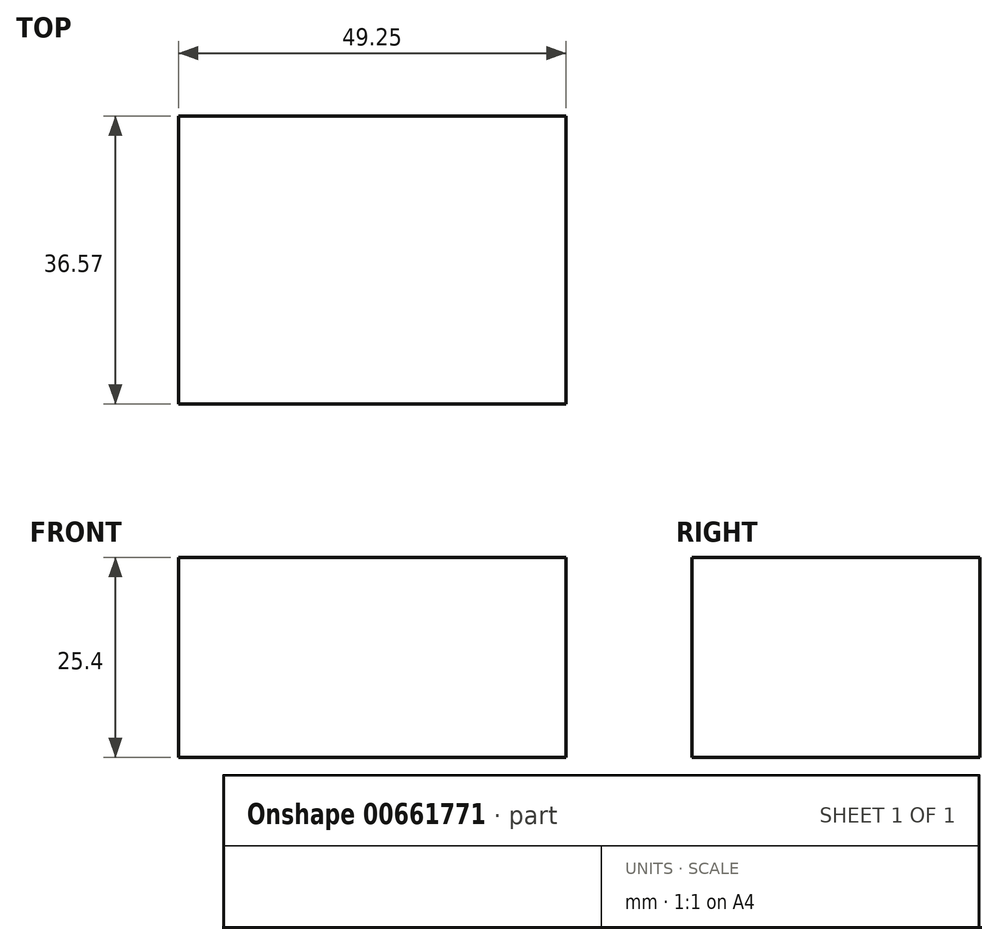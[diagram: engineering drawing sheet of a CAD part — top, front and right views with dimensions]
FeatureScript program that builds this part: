
annotation { "Feature Type Name" : "Feature", "Feature Type Description" : "" }
export const myFeature = defineFeature(function(context is Context, id is Id, definition is map)
    precondition{}
    {
        {
            var Q0;
            Q0=qCreatedBy(makeId("Top.planeOp"),FACE);
            var sketch = newSketch(context, id + "F0", { "sketchPlane" : qUnion([Q0])});
            skLineSegment(sketch, "E0.bottom", {"start": v(0, 0) * mm, "end": v(49.25, 0) * mm});
            skLineSegment(sketch, "E0.top", {"start": v(0, -36.57) * mm, "end": v(49.25, -36.57) * mm});
            skLineSegment(sketch, "E0.left", {"start": v(0, 0) * mm, "end": v(0, -36.57) * mm});
            skLineSegment(sketch, "E0.right", {"start": v(49.25, 0) * mm, "end": v(49.25, -36.57) * mm});
            skSolve(sketch);
        }
        {
            var Q0;
            Q0 = qSketchRegion(id + "F0", true);
            extrude(context, id + "F1", {"entities" : qUnion([Q0]), "depth" : 25.4 * mm, "offsetDistance" : 25.4 * mm});
        }
    });
